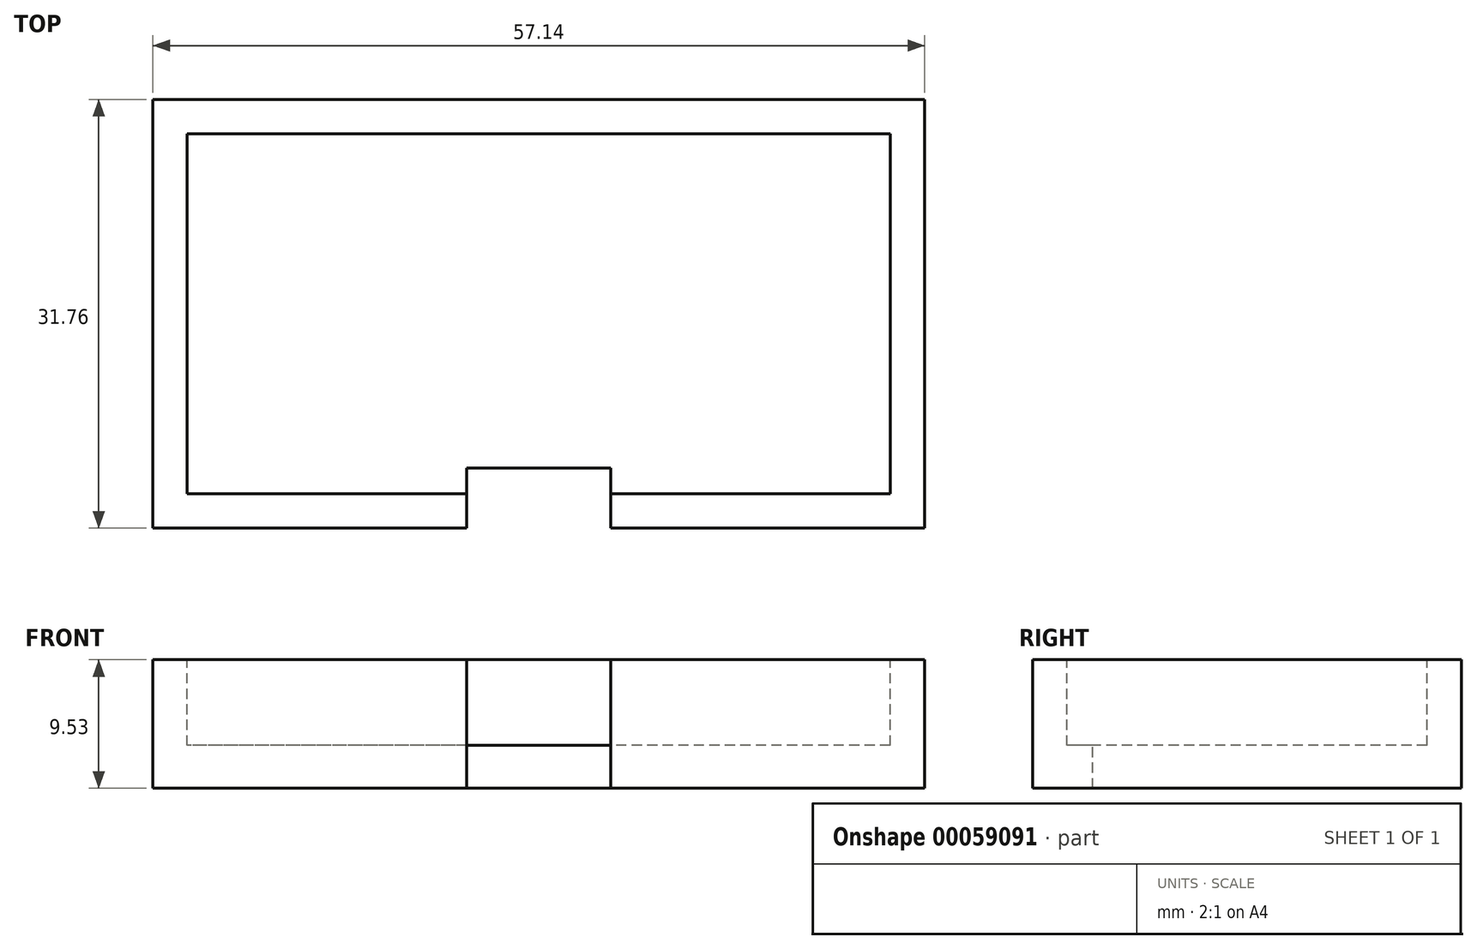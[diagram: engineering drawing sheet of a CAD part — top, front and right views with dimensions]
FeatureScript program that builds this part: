
annotation { "Feature Type Name" : "Feature", "Feature Type Description" : "" }
export const myFeature = defineFeature(function(context is Context, id is Id, definition is map)
    precondition{}
    {
        {
            var Q0;
            Q0=qCreatedBy(makeId("Top.planeOp"),FACE);
            var sketch = newSketch(context, id + "F0", { "sketchPlane" : qUnion([Q0])});
            skLineSegment(sketch, "E0.rect.bottom", {"start": v(-28.57, 15.88) * mm, "end": v(28.58, 15.88) * mm});
            skLineSegment(sketch, "E0.rect.top", {"start": v(-28.58, -15.87) * mm, "end": v(28.57, -15.87) * mm});
            skLineSegment(sketch, "E0.rect.left", {"start": v(-28.57, 15.88) * mm, "end": v(-28.58, -15.87) * mm});
            skLineSegment(sketch, "E0.rect.right", {"start": v(28.58, 15.88) * mm, "end": v(28.57, -15.87) * mm});
            skPoint(sketch, "E0.rect.middle", {"position": v(0, 0) * mm});
            skSolve(sketch);
        }
        {
            var Q0;
            Q0=makeQuery(id+"F0.imprint","IMPRINT",FACE,{"disambiguationData":[TD([[makeQuery(id+"F0.imprint","IMPRINT",EDGE,{"derivedFrom":sQuery(id+"F0.wireOp",EDGE,"E0.rect.bottom")}),-1.0]])]});
            extrude(context, id + "F1", {"entities" : qUnion([Q0]), "depth" : 9.52 * mm});
        }
        {
            var Q0;
            Q0=makeQuery(id+"F1.opExtrude","CAP_FACE",FACE,{"disambiguationData":[OSD([sQuery(id+"F0.wireOp",EDGE,"E0.rect.bottom"),sQuery(id+"F0.wireOp",EDGE,"E0.rect.top"),sQuery(id+"F0.wireOp",EDGE,"E0.rect.left"),sQuery(id+"F0.wireOp",EDGE,"E0.rect.right")])],"isStart":false});
            var sketch = newSketch(context, id + "F2", { "sketchPlane" : qUnion([Q0])});
            skLineSegment(sketch, "E1.rect.bottom", {"start": v(26.04, 13.33) * mm, "end": v(-26.04, 13.33) * mm});
            skLineSegment(sketch, "E1.rect.top", {"start": v(26.04, -13.33) * mm, "end": v(-26.04, -13.33) * mm});
            skLineSegment(sketch, "E1.rect.left", {"start": v(26.04, 13.34) * mm, "end": v(26.04, -13.34) * mm});
            skLineSegment(sketch, "E1.rect.right", {"start": v(-26.04, 13.34) * mm, "end": v(-26.04, -13.34) * mm});
            skPoint(sketch, "E1.rect.middle", {"position": v(0, 0) * mm});
            skSolve(sketch);
        }
        {
            var Q0;
            Q0=makeQuery(id+"F2.imprint","IMPRINT",FACE,{"disambiguationData":[TD([[makeQuery(id+"F2.imprint","IMPRINT",EDGE,{"derivedFrom":sQuery(id+"F2.wireOp",EDGE,"E1.rect.bottom")}),1.0]])]});
            extrude(context, id + "F3", {"entities" : qUnion([Q0]), "operationType" : NewBodyOperationType.REMOVE, "oppositeDirection" : true, "depth" : 6.35 * mm});
        }
        {
            var Q0;
            Q0=makeQuery(id+"F1.opExtrude","CAP_FACE",FACE,{"disambiguationData":[OSD([sQuery(id+"F0.wireOp",EDGE,"E0.rect.bottom"),sQuery(id+"F0.wireOp",EDGE,"E0.rect.top"),sQuery(id+"F0.wireOp",EDGE,"E0.rect.left"),sQuery(id+"F0.wireOp",EDGE,"E0.rect.right")])],"isStart":false});
            var sketch = newSketch(context, id + "F4", { "sketchPlane" : qUnion([Q0])});
            skLineSegment(sketch, "E2.rect.bottom", {"start": v(5.33, -11.43) * mm, "end": v(-5.33, -11.43) * mm});
            skLineSegment(sketch, "E2.rect.top", {"start": v(5.33, -16.5) * mm, "end": v(-5.33, -16.5) * mm});
            skLineSegment(sketch, "E2.rect.left", {"start": v(5.33, -11.43) * mm, "end": v(5.33, -16.5) * mm});
            skLineSegment(sketch, "E2.rect.right", {"start": v(-5.33, -11.43) * mm, "end": v(-5.33, -16.5) * mm});
            skPoint(sketch, "E2.rect.middle", {"position": v(0, -13.97) * mm});
            skSolve(sketch);
        }
        {
            var Q0;
            {var subQ0=sQuery(id+"F4.wireOp",EDGE,"E2.rect.left");var subQ1=makeQuery(id+"F1.opExtrude","CAP_EDGE",EDGE,{"disambiguationData":[OSD([sQuery(id+"F0.wireOp",EDGE,"E0.rect.top")])],"isStart":false});var subQ2=makeQuery(id+"F4.imprint","INTERSECT",VERTEX,{"derivedFrom":[subQ1,subQ0]});Q0=makeQuery(id+"F4.imprint","IMPRINT",FACE,{"disambiguationData":[TD([[makeQuery(id+"F4.imprint","IMPRINT",EDGE,{"disambiguationData":[TD([[subQ2,1.0]])],"derivedFrom":subQ0}),-1.0]])]});}
            var Q1;
            {var subQ0=sQuery(id+"F4.wireOp",EDGE,"E2.rect.bottom");Q1=makeQuery(id+"F4.imprint","IMPRINT",FACE,{"disambiguationData":[TD([[makeQuery(id+"F4.imprint","IMPRINT",EDGE,{"derivedFrom":subQ0}),1.0]])]});}
            extrude(context, id + "F5", {"entities" : qUnion([Q0, Q1]), "operationType" : NewBodyOperationType.REMOVE, "oppositeDirection" : true, "depth" : 25.4 * mm});
        }
    });
